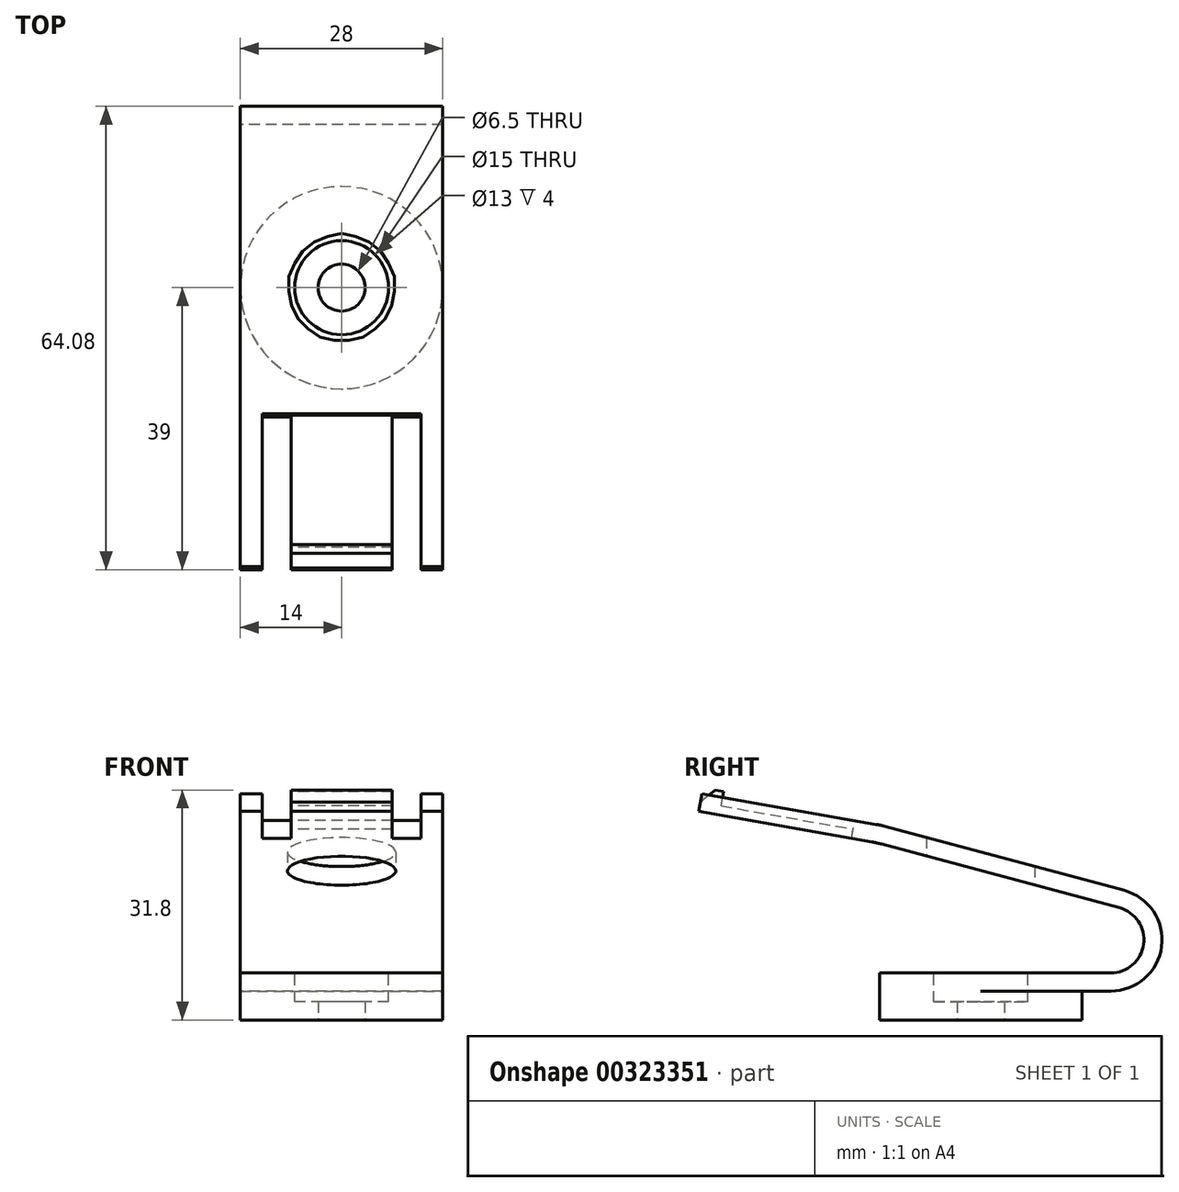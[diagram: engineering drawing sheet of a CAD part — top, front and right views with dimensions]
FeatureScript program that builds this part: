
annotation { "Feature Type Name" : "Feature", "Feature Type Description" : "" }
export const myFeature = defineFeature(function(context is Context, id is Id, definition is map)
    precondition{}
    {
        {
            var Q0;
            Q0=qCreatedBy(makeId("Right.planeOp"),FACE);
            var sketch = newSketch(context, id + "F0", { "sketchPlane" : qUnion([Q0])});
            skLineSegment(sketch, "E0", {"start": v(-32, 0) * mm, "end": v(0, 0) * mm});
            skArc(sketch, "E1", {"start": v(0, 0) * mm, "mid": v(4.54, 3.98) * mm, "end": v(1.19, 9) * mm});
            skLineSegment(sketch, "E2", {"start": v(1.19, 9) * mm, "end": v(-32.38, 18) * mm});
            skLineSegment(sketch, "E3", {"start": v(-32.38, 18) * mm, "end": v(-57, 22.34) * mm});
            skLineSegment(sketch, "E4.0", {"start": v(-31.84, 20.44) * mm, "end": v(-56.57, 24.8) * mm});
            skLineSegment(sketch, "E4.1", {"start": v(1.83, 11.42) * mm, "end": v(-31.84, 20.44) * mm});
            skArc(sketch, "E4.2", {"start": v(0, -2.5) * mm, "mid": v(7.02, 3.66) * mm, "end": v(1.83, 11.42) * mm});
            skLineSegment(sketch, "E4.3", {"start": v(-32, -2.5) * mm, "end": v(0, -2.5) * mm});
            skLineSegment(sketch, "E5", {"start": v(-56.57, 24.8) * mm, "end": v(-57, 22.34) * mm});
            skLineSegment(sketch, "E6", {"start": v(-32, -2.5) * mm, "end": v(-32, 0) * mm});
            skSolve(sketch);
        }
        {
            var Q0;
            Q0 = qSketchRegion(id + "F0", true);
            extrude(context, id + "F1", {"entities" : qUnion([Q0]), "depth" : 28 * mm, "offsetDistance" : 25 * mm});
        }
        {
            var Q0;
            Q0=makeQuery(id+"F1.opExtrude","SWEPT_EDGE",EDGE,{"disambiguationData":[OSD([sQuery(id+"F0.wireOp",EDGE,"E4.0"),sQuery(id+"F0.wireOp",EDGE,"E4.1")])]});
            var Q1;
            Q1=makeQuery(id+"F1.opExtrude","SWEPT_EDGE",EDGE,{"disambiguationData":[OSD([sQuery(id+"F0.wireOp",EDGE,"E2"),sQuery(id+"F0.wireOp",EDGE,"E3")])]});
            fillet(context, id + "F2", {"entities" : qUnion([Q0, Q1]), "tangentPropagation" : true, "radius" : 15 * mm, "defaultsChanged" : true, "vertexSettings" : [], "allowEdgeOverflow" : false});
        }
        {
            var Q0;
            Q0=makeQuery(id+"F1.opExtrude","SWEPT_FACE",FACE,{"disambiguationData":[OSD([sQuery(id+"F0.wireOp",EDGE,"E4.3")])]});
            var sketch = newSketch(context, id + "F3", { "sketchPlane" : qUnion([Q0])});
            skCircle(sketch, "E7", {"center": v(14, 18) * mm, "radius": 14 * mm});
            skLineSegment(sketch, "E8", {"start": v(14, 41.31) * mm, "end": v(14, -18.09) * mm, "construction": true});
            skSolve(sketch);
        }
        {
            var Q0;
            Q0 = qSketchRegion(id + "F3", true);
            extrude(context, id + "F4", {"entities" : qUnion([Q0]), "operationType" : NewBodyOperationType.ADD, "depth" : 4 * mm, "offsetDistance" : 25 * mm});
        }
        {
            var Q0;
            {var subQ0=sQuery(id+"F0.wireOp",EDGE,"E6");var subQ1=sQuery(id+"F0.wireOp",EDGE,"E4.3");var subQ2=makeQuery(id+"F1.opExtrude","SWEPT_FACE",FACE,{"disambiguationData":[OSD([subQ1])]});Q0=makeQuery(id+"F4.boolean.opBoolean","SPLIT",FACE,{"disambiguationData":[TD([makeQuery(id+"F1.opExtrude","CAP_FACE",FACE,{"disambiguationData":[OSD([sQuery(id+"F0.wireOp",EDGE,"E0"),sQuery(id+"F0.wireOp",EDGE,"E1"),sQuery(id+"F0.wireOp",EDGE,"E2"),sQuery(id+"F0.wireOp",EDGE,"E3"),sQuery(id+"F0.wireOp",EDGE,"E4.0"),sQuery(id+"F0.wireOp",EDGE,"E4.1"),sQuery(id+"F0.wireOp",EDGE,"E4.2"),subQ1,sQuery(id+"F0.wireOp",EDGE,"E5"),subQ0])],"isStart":false}),subQ2,makeQuery(id+"F1.opExtrude","SWEPT_FACE",FACE,{"disambiguationData":[OSD([subQ0])]}),makeQuery(id+"F4.opExtrude","SWEPT_FACE",FACE,{"disambiguationData":[OSD([sQuery(id+"F3.wireOp",EDGE,"E7")])]})])],"derivedFrom":subQ2});}
            var sketch = newSketch(context, id + "F5", { "sketchPlane" : qUnion([Q0])});
            skLineSegment(sketch, "E9.0", {"start": v(28, 32) * mm, "end": v(28, 18) * mm});
            skLineSegment(sketch, "E9.1", {"start": v(28, 32) * mm, "end": v(14, 32) * mm});
            skLineSegment(sketch, "E10.0", {"start": v(14, 32) * mm, "end": v(0, 32) * mm});
            skLineSegment(sketch, "E10.1", {"start": v(0, 32) * mm, "end": v(0, 18) * mm});
            skArc(sketch, "E11", {"start": v(28, 18) * mm, "mid": v(23.9, 27.9) * mm, "end": v(14, 32) * mm});
            skArc(sketch, "E12", {"start": v(14, 32) * mm, "mid": v(4.1, 27.9) * mm, "end": v(0, 18) * mm});
            skSolve(sketch);
        }
        {
            var Q0;
            Q0 = qSketchRegion(id + "F5", true);
            extrude(context, id + "F6", {"entities" : qUnion([Q0]), "operationType" : NewBodyOperationType.REMOVE, "endBound" : BoundingType.UP_TO_NEXT, "oppositeDirection" : true, "depth" : 25 * mm, "offsetDistance" : 25 * mm});
        }
        {
            var Q0;
            Q0=makeQuery(id+"F4.opExtrude","CAP_FACE",FACE,{"disambiguationData":[OSD([sQuery(id+"F3.wireOp",EDGE,"E7")])],"isStart":false});
            var sketch = newSketch(context, id + "F7", { "sketchPlane" : qUnion([Q0])});
            skCircle(sketch, "E13", {"center": v(14, 18) * mm, "radius": 3.25 * mm});
            skSolve(sketch);
        }
        {
            var Q0;
            Q0 = qSketchRegion(id + "F7", true);
            extrude(context, id + "F8", {"entities" : qUnion([Q0]), "operationType" : NewBodyOperationType.REMOVE, "endBound" : BoundingType.THROUGH_ALL, "oppositeDirection" : true, "depth" : 25 * mm, "offsetDistance" : 25 * mm});
        }
        {
            var Q0;
            Q0=makeQuery(id+"F1.opExtrude","SWEPT_FACE",FACE,{"disambiguationData":[OSD([sQuery(id+"F0.wireOp",EDGE,"E0")])]});
            var sketch = newSketch(context, id + "F9", { "sketchPlane" : qUnion([Q0])});
            skCircle(sketch, "E14", {"center": v(14, -18) * mm, "radius": 7.5 * mm});
            skSolve(sketch);
        }
        {
            var Q0;
            Q0 = qSketchRegion(id + "F9", true);
            extrude(context, id + "F10", {"entities" : qUnion([Q0]), "operationType" : NewBodyOperationType.REMOVE, "endBound" : BoundingType.THROUGH_ALL, "depth" : 25 * mm, "offsetDistance" : 25 * mm});
        }
        {
            var Q0;
            Q0=makeQuery(id+"F1.opExtrude","SWEPT_FACE",FACE,{"disambiguationData":[OSD([sQuery(id+"F0.wireOp",EDGE,"E0")])]});
            var sketch = newSketch(context, id + "F11", { "sketchPlane" : qUnion([Q0])});
            skCircle(sketch, "E15", {"center": v(14, -18) * mm, "radius": 6.5 * mm});
            skSolve(sketch);
        }
        {
            var Q0;
            Q0 = qSketchRegion(id + "F11", true);
            extrude(context, id + "F12", {"entities" : qUnion([Q0]), "operationType" : NewBodyOperationType.REMOVE, "oppositeDirection" : true, "depth" : 4 * mm, "offsetDistance" : 25 * mm});
        }
        {
            var Q0;
            Q0=makeQuery(id+"F1.opExtrude","SWEPT_FACE",FACE,{"disambiguationData":[OSD([sQuery(id+"F0.wireOp",EDGE,"E4.0")])]});
            var sketch = newSketch(context, id + "F13", { "sketchPlane" : qUnion([Q0])});
            skLineSegment(sketch, "E16", {"start": v(14, -75.78) * mm, "end": v(14, -31.02) * mm, "construction": true});
            skLineSegment(sketch, "E17.bottom", {"start": v(25, -60.01) * mm, "end": v(21, -60.01) * mm});
            skLineSegment(sketch, "E17.top", {"start": v(25, -38.56) * mm, "end": v(21, -38.56) * mm});
            skLineSegment(sketch, "E17.left", {"start": v(25, -60.01) * mm, "end": v(25, -38.56) * mm});
            skLineSegment(sketch, "E17.right", {"start": v(21, -60.01) * mm, "end": v(21, -38.56) * mm});
            skLineSegment(sketch, "E18.MirrorCS", {"start": v(3, -60.01) * mm, "end": v(7, -60.01) * mm});
            skLineSegment(sketch, "E19.MirrorCS", {"start": v(7, -60.01) * mm, "end": v(7, -38.56) * mm});
            skLineSegment(sketch, "E20.MirrorCS", {"start": v(3, -60.01) * mm, "end": v(3, -38.56) * mm});
            skLineSegment(sketch, "E21.MirrorCS", {"start": v(3, -38.56) * mm, "end": v(7, -38.56) * mm});
            skSolve(sketch);
        }
        {
            var Q0;
            Q0 = qSketchRegion(id + "F13", true);
            extrude(context, id + "F14", {"entities" : qUnion([Q0]), "operationType" : NewBodyOperationType.REMOVE, "endBound" : BoundingType.UP_TO_NEXT, "oppositeDirection" : true, "depth" : 25 * mm, "offsetDistance" : 25 * mm});
        }
        {
            var Q0;
            Q0=makeQuery(id+"F1.opExtrude","SWEPT_FACE",FACE,{"disambiguationData":[OSD([sQuery(id+"F0.wireOp",EDGE,"E4.0")])]});
            var sketch = newSketch(context, id + "F15", { "sketchPlane" : qUnion([Q0])});
            skLineSegment(sketch, "E22.bottom", {"start": v(21, -60.01) * mm, "end": v(7, -60.01) * mm});
            skLineSegment(sketch, "E22.top", {"start": v(21, -38.56) * mm, "end": v(7, -38.56) * mm});
            skLineSegment(sketch, "E22.left", {"start": v(21, -60.01) * mm, "end": v(21, -38.56) * mm});
            skLineSegment(sketch, "E22.right", {"start": v(7, -60.01) * mm, "end": v(7, -38.56) * mm});
            skSolve(sketch);
        }
        {
            var Q0;
            Q0 = qSketchRegion(id + "F15", true);
            extrude(context, id + "F16", {"entities" : qUnion([Q0]), "operationType" : NewBodyOperationType.REMOVE, "oppositeDirection" : true, "depth" : 1.2 * mm, "offsetDistance" : 25 * mm});
        }
        {
            var Q0;
            Q0=makeQuery(id+"F14.boolean.opBoolean","COPY",FACE,{"derivedFrom":makeQuery(id+"F14.opExtrude","SWEPT_FACE",FACE,{"disambiguationData":[OSD([sQuery(id+"F13.wireOp",EDGE,"E19.MirrorCS")])]})});
            var sketch = newSketch(context, id + "F17", { "sketchPlane" : qUnion([Q0])});
            skLineSegment(sketch, "E23", {"start": v(53.92, 23.12) * mm, "end": v(53.57, 25.09) * mm});
            skLineSegment(sketch, "E24", {"start": v(54.75, 25.3) * mm, "end": v(56.77, 23.62) * mm});
            skLineSegment(sketch, "E25", {"start": v(53.92, 23.12) * mm, "end": v(56.77, 23.62) * mm});
            skLineSegment(sketch, "E26", {"start": v(53.57, 25.09) * mm, "end": v(54.75, 25.3) * mm});
            skSolve(sketch);
        }
        {
            var Q0;
            Q0 = qSketchRegion(id + "F17", true);
            var Q1;
            Q1=makeQuery(id+"F14.boolean.opBoolean","COPY",FACE,{"derivedFrom":makeQuery(id+"F14.opExtrude","SWEPT_FACE",FACE,{"disambiguationData":[OSD([sQuery(id+"F13.wireOp",EDGE,"E17.right")])]})});
            extrude(context, id + "F18", {"entities" : qUnion([Q0]), "operationType" : NewBodyOperationType.ADD, "endBound" : BoundingType.UP_TO_SURFACE, "oppositeDirection" : true, "depth" : 25 * mm, "endBoundEntityFace" : qUnion([Q1]), "offsetDistance" : 25 * mm});
        }
    });
